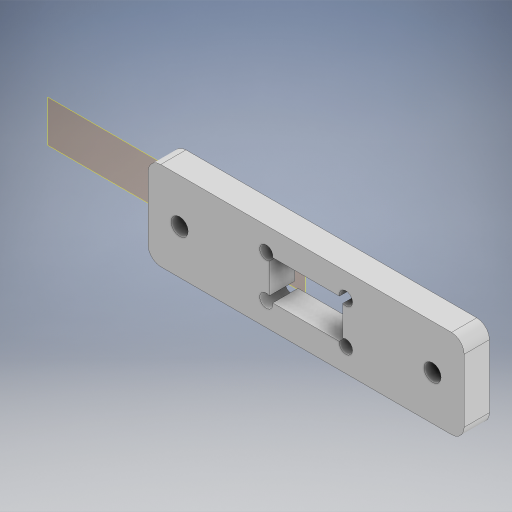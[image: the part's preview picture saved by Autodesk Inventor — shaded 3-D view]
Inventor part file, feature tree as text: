
AUTODESK INVENTOR PART (.ipt)
format: ipt  version: 2024 (Build 280153000, 153)  size: 337,920 bytes
history: native  units: mm
features: other x5, sketch x3, reference x3, extrude x2, projected_geometry x2, fillet x1, hole x1
ambient origin geometry x8: Origin, YZ Plane, XZ Plane, XY Plane, X Axis, Y Axis, Z Axis, Center Point
bodies: Body1 (feature_tree)
feature tree (17):
  other  "솔리드1"
  other  "작업 평면1"
  extrude  "돌출1"  Depth=0.3mm
  fillet  "모깎기1"  Radius=4.0mm
  extrude  "돌출2"  Depth=10.0mm
  hole  "구멍1"  [1 undecoded]
  sketch  "스케치1"
  reference  "참조1"
  reference  "참조2"
  reference  "참조3"
  sketch  "스케치2"
  projected_geometry  "투영된 루프1"
  sketch  "스케치3"
  projected_geometry  "투영된 루프2"
  other  "<userpath>\Desktop\ZIG\조립품1.iam"
  other  "조립품1.iam"
  other  "head:1"
note: 1 required parameter value undecoded (feature->parameter linkage not recoverable at this tier; creation-order binding heuristic only, values carry confidence <= 0.55)
